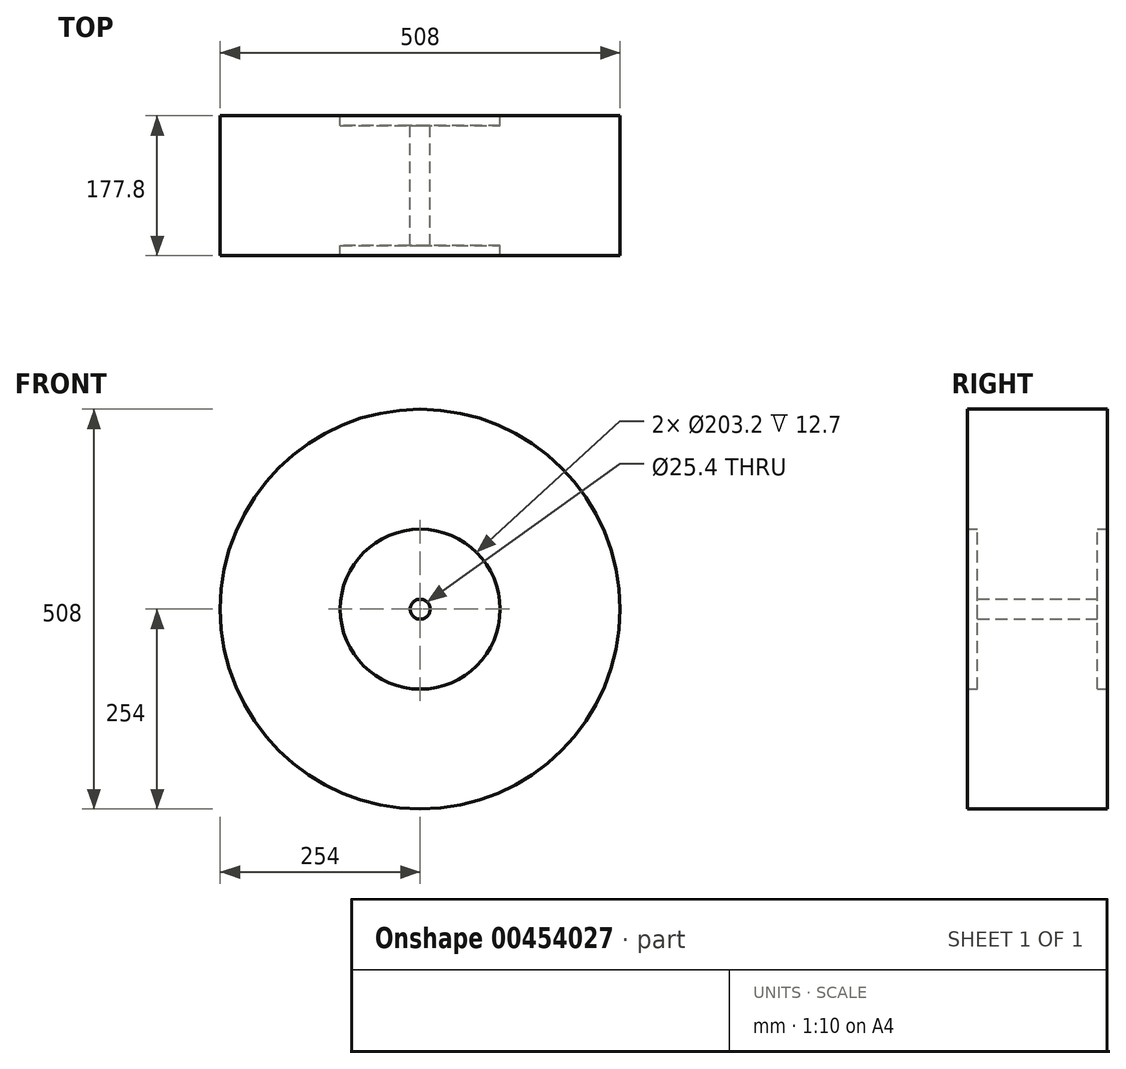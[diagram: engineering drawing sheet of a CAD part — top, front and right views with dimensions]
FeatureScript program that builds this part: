
annotation { "Feature Type Name" : "Feature", "Feature Type Description" : "" }
export const myFeature = defineFeature(function(context is Context, id is Id, definition is map)
    precondition{}
    {
        {
            var Q0;
            Q0=qCreatedBy(makeId("Front.planeOp"),FACE);
            var sketch = newSketch(context, id + "F0", { "sketchPlane" : qUnion([Q0])});
            skCircle(sketch, "E0", {"center": v(0, 0) * mm, "radius": 254 * mm});
            skCircle(sketch, "E1", {"center": v(0, 0) * mm, "radius": 101.6 * mm});
            skCircle(sketch, "E2", {"center": v(0, 0) * mm, "radius": 12.7 * mm});
            skSolve(sketch);
        }
        {
            var Q0;
            Q0=makeQuery(id+"F0.imprint","IMPRINT",FACE,{"disambiguationData":[TD([[makeQuery(id+"F0.imprint","IMPRINT",EDGE,{"derivedFrom":sQuery(id+"F0.wireOp",EDGE,"E0")}),1.0]])]});
            extrude(context, id + "F1", {"entities" : qUnion([Q0]), "endBound" : BoundingType.SYMMETRIC, "depth" : 177.8 * mm});
        }
        {
            var Q0;
            Q0=qCreatedBy(makeId("Front.planeOp"),FACE);
            var sketch = newSketch(context, id + "F2", { "sketchPlane" : qUnion([Q0])});
            skCircle(sketch, "E3", {"center": v(0, 0) * mm, "radius": 101.6 * mm});
            skSolve(sketch);
        }
        {
            var Q0;
            Q0=makeQuery(id+"F2.imprint","IMPRINT",FACE,{"disambiguationData":[TD([[makeQuery(id+"F2.imprint","IMPRINT",EDGE,{"derivedFrom":sQuery(id+"F2.wireOp",EDGE,"E3")}),1.0]])]});
            extrude(context, id + "F3", {"entities" : qUnion([Q0]), "operationType" : NewBodyOperationType.ADD, "endBound" : BoundingType.SYMMETRIC, "depth" : 152.4 * mm});
        }
        {
            var Q0;
            Q0=makeQuery(id+"F3.opExtrude","CAP_FACE",FACE,{"disambiguationData":[OSD([sQuery(id+"F2.wireOp",EDGE,"E3")])],"isStart":false});
            var sketch = newSketch(context, id + "F4", { "sketchPlane" : qUnion([Q0])});
            skCircle(sketch, "E4", {"center": v(0, 0) * mm, "radius": 12.7 * mm});
            skSolve(sketch);
        }
        {
            var Q0;
            Q0=makeQuery(id+"F4.imprint","IMPRINT",FACE,{"disambiguationData":[TD([[makeQuery(id+"F4.imprint","IMPRINT",EDGE,{"derivedFrom":sQuery(id+"F4.wireOp",EDGE,"E4")}),1.0]])]});
            extrude(context, id + "F5", {"entities" : qUnion([Q0]), "operationType" : NewBodyOperationType.REMOVE, "endBound" : BoundingType.SYMMETRIC, "depth" : 304.8 * mm});
        }
    });
